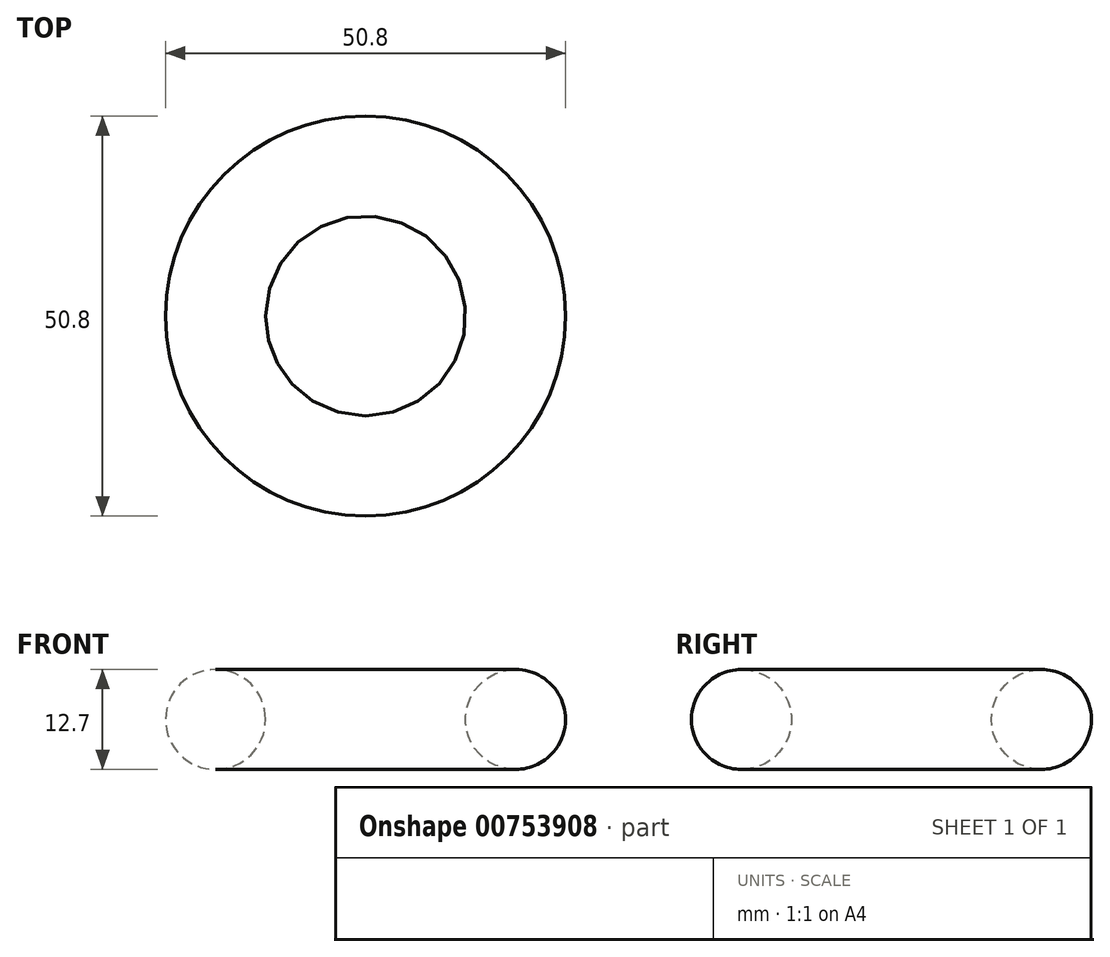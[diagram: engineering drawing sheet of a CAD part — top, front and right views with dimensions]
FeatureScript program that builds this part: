
annotation { "Feature Type Name" : "Feature", "Feature Type Description" : "" }
export const myFeature = defineFeature(function(context is Context, id is Id, definition is map)
    precondition{}
    {
        {
            var Q0;
            Q0=qCreatedBy(makeId("Front.planeOp"),FACE);
            var sketch = newSketch(context, id + "F0", { "sketchPlane" : qUnion([Q0])});
            skLineSegment(sketch, "E0", {"start": v(0, 0) * mm, "end": v(0, 12.7) * mm, "construction": true});
            skLineSegment(sketch, "E1.bottom", {"start": v(12.7, 0) * mm, "end": v(25.4, 0) * mm});
            skLineSegment(sketch, "E1.top", {"start": v(12.7, 12.7) * mm, "end": v(25.4, 12.7) * mm});
            skLineSegment(sketch, "E1.left", {"start": v(12.7, 0) * mm, "end": v(12.7, 12.7) * mm});
            skLineSegment(sketch, "E1.right", {"start": v(25.4, 0) * mm, "end": v(25.4, 12.7) * mm});
            skSolve(sketch);
        }
        {
            var Q0;
            Q0=makeQuery(id+"F0.imprint","IMPRINT",FACE,{"disambiguationData":[TD([[makeQuery(id+"F0.imprint","IMPRINT",EDGE,{"derivedFrom":sQuery(id+"F0.wireOp",EDGE,"E1.bottom")}),1.0]])]});
            var Q1;
            Q1=sQuery(id+"F0.wireOp",EDGE,"E0");
            revolve(context, id + "F1", {"surfaceOperationType" : NewSurfaceOperationType.NEW, "entities" : qUnion([Q0]), "axis" : qUnion([Q1]), "revolveType" : RevolveType.FULL});
        }
        {
            var Q0;
            Q0=makeQuery(id+"F1.opRevolve","SWEPT_FACE",FACE,{"disambiguationData":[OSD([sQuery(id+"F0.wireOp",EDGE,"E1.top")])]});
            var Q1;
            Q1=makeQuery(id+"F1.opRevolve","SWEPT_FACE",FACE,{"disambiguationData":[OSD([sQuery(id+"F0.wireOp",EDGE,"E1.bottom")])]});
            fillet(context, id + "F2", {"entities" : qUnion([Q0, Q1]), "radius" : 6.35 * mm, "tangentPropagation" : true, "allowEdgeOverflow" : false});
        }
    });
